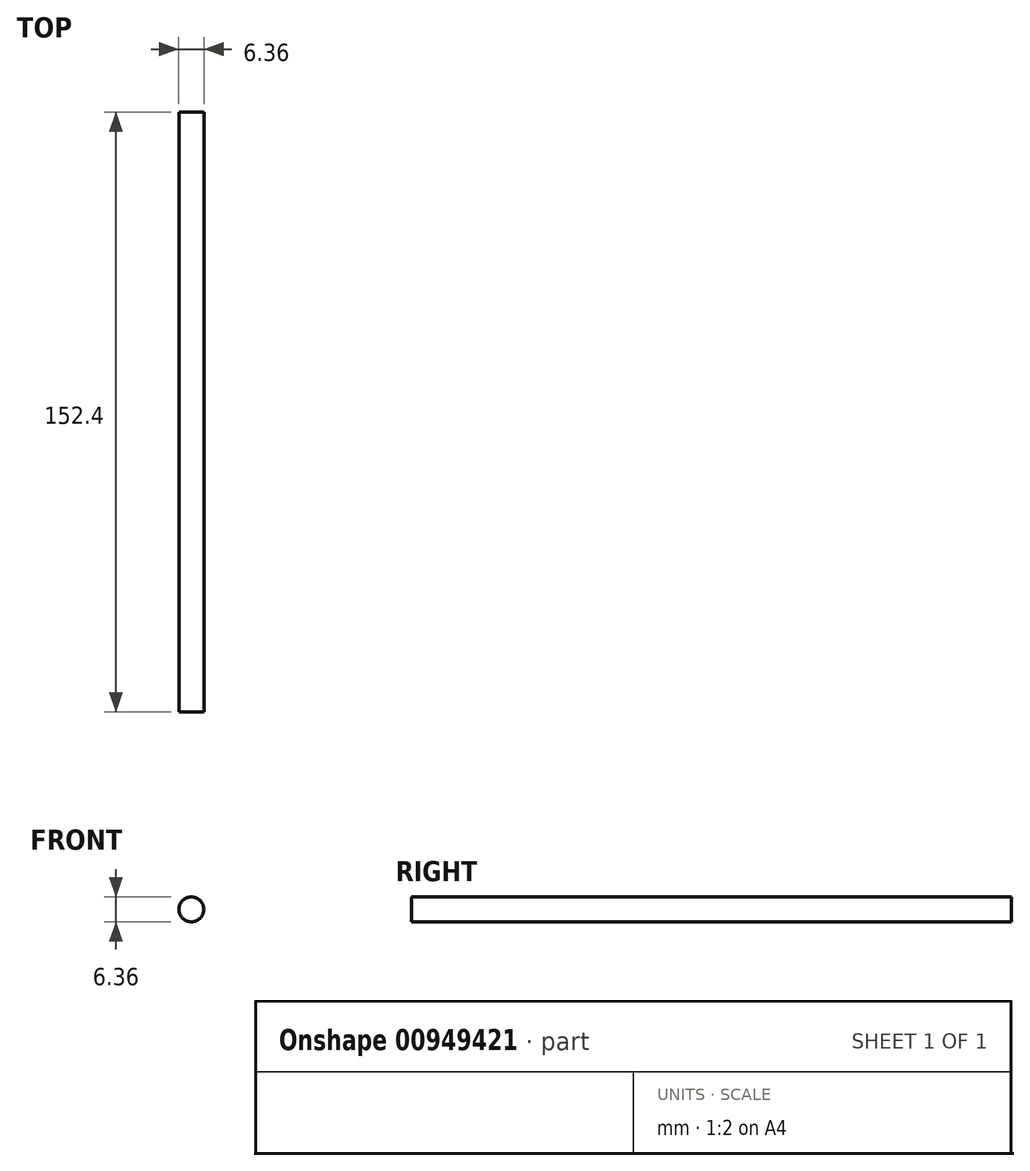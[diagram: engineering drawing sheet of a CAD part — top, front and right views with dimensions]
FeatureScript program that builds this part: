
annotation { "Feature Type Name" : "Feature", "Feature Type Description" : "" }
export const myFeature = defineFeature(function(context is Context, id is Id, definition is map)
    precondition{}
    {
        {
            var Q0;
            Q0=qCreatedBy(makeId("Front.planeOp"),FACE);
            var sketch = newSketch(context, id + "F0", { "sketchPlane" : qUnion([Q0])});
            skCircle(sketch, "E0", {"center": v(0, 0) * mm, "radius": 3.18 * mm});
            skSolve(sketch);
        }
        {
            var Q0;
            Q0=makeQuery(id+"F0.imprint","IMPRINT",FACE,{"disambiguationData":[TD([[makeQuery(id+"F0.imprint","IMPRINT",EDGE,{"derivedFrom":sQuery(id+"F0.wireOp",EDGE,"E0")}),1.0]])]});
            extrude(context, id + "F1", {"entities" : qUnion([Q0]), "endBound" : BoundingType.SYMMETRIC, "depth" : 152.4 * mm, "offsetDistance" : 25.4 * mm});
        }
    });
